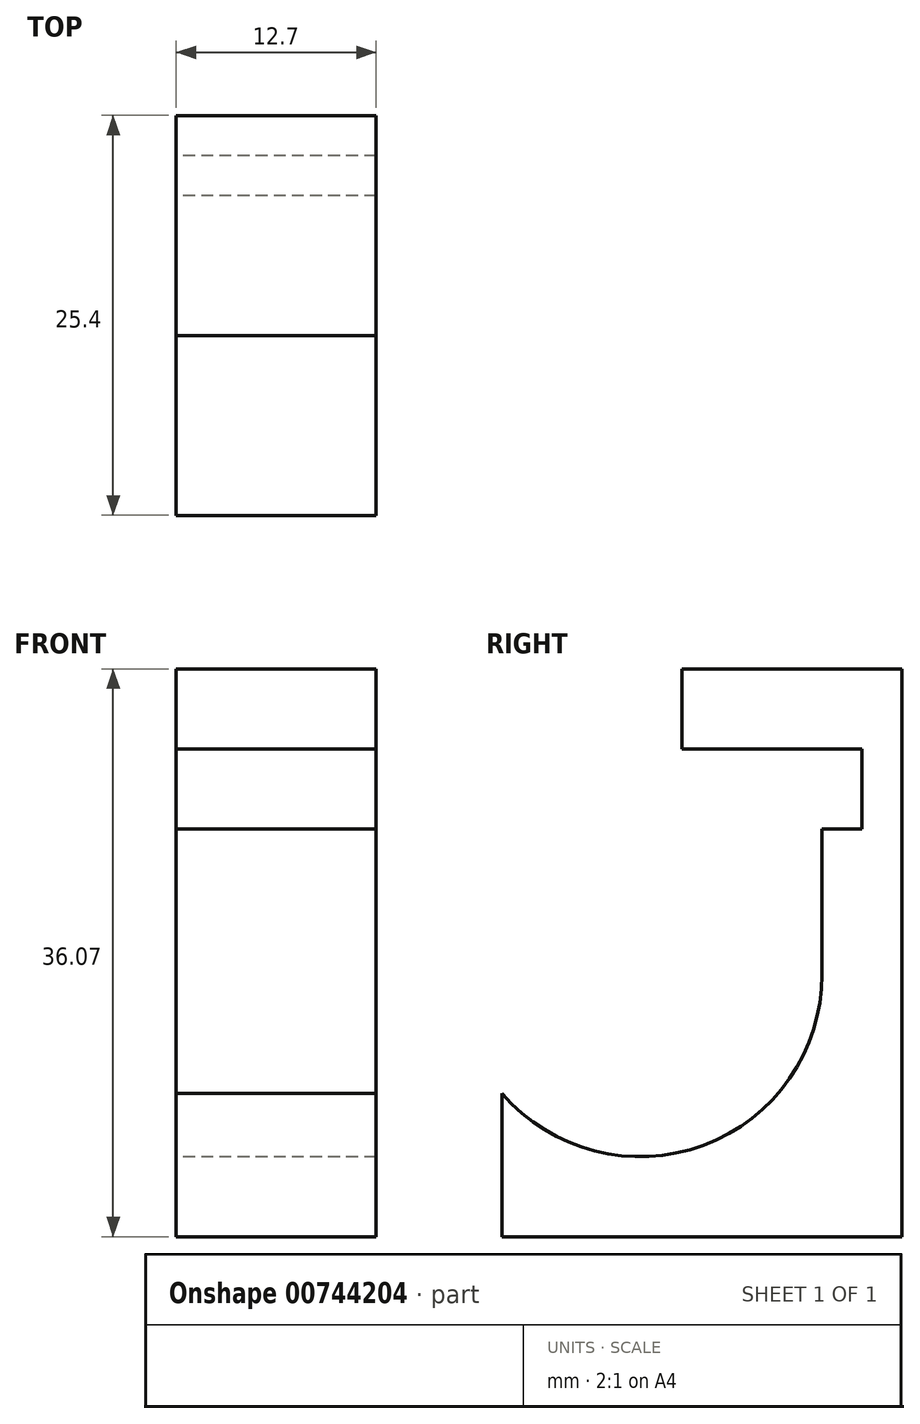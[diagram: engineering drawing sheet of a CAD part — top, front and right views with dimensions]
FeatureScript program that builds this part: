
annotation { "Feature Type Name" : "Feature", "Feature Type Description" : "" }
export const myFeature = defineFeature(function(context is Context, id is Id, definition is map)
    precondition{}
    {
        {
            var Q0;
            Q0=qCreatedBy(makeId("Right.planeOp"),FACE);
            var sketch = newSketch(context, id + "F0", { "sketchPlane" : qUnion([Q0])});
            skArc(sketch, "E0", {"start": v(-8.76, -7.53) * mm, "mid": v(4.02, -10.84) * mm, "end": v(11.56, 0) * mm});
            skLineSegment(sketch, "E1", {"start": v(-8.76, -7.53) * mm, "end": v(-8.76, -16.64) * mm});
            skLineSegment(sketch, "E2", {"start": v(-8.76, -16.64) * mm, "end": v(11.56, -16.64) * mm});
            skLineSegment(sketch, "E3", {"start": v(11.56, 0) * mm, "end": v(11.56, 9.27) * mm});
            skLineSegment(sketch, "E4", {"start": v(11.56, 9.27) * mm, "end": v(14.1, 9.27) * mm});
            skLineSegment(sketch, "E5", {"start": v(14.1, 9.27) * mm, "end": v(14.1, 14.35) * mm});
            skLineSegment(sketch, "E6", {"start": v(14.1, 14.35) * mm, "end": v(11.56, 14.35) * mm});
            skLineSegment(sketch, "E7", {"start": v(11.56, 14.35) * mm, "end": v(2.67, 14.35) * mm});
            skLineSegment(sketch, "E8", {"start": v(2.67, 14.35) * mm, "end": v(2.67, 19.43) * mm});
            skLineSegment(sketch, "E9", {"start": v(2.67, 19.43) * mm, "end": v(16.64, 19.43) * mm});
            skLineSegment(sketch, "E10", {"start": v(16.64, 19.43) * mm, "end": v(16.64, -16.64) * mm});
            skLineSegment(sketch, "E11", {"start": v(16.64, -16.64) * mm, "end": v(11.56, -16.64) * mm});
            skSolve(sketch);
        }
        {
            var Q0;
            Q0=makeQuery(id+"F0.imprint","IMPRINT",FACE,{"disambiguationData":[TD([[makeQuery(id+"F0.imprint","IMPRINT",EDGE,{"derivedFrom":sQuery(id+"F0.wireOp",EDGE,"E0")}),-1.0]])]});
            extrude(context, id + "F1", {"entities" : qUnion([Q0]), "depth" : 12.7 * mm, "offsetDistance" : 25.4 * mm});
        }
    });
